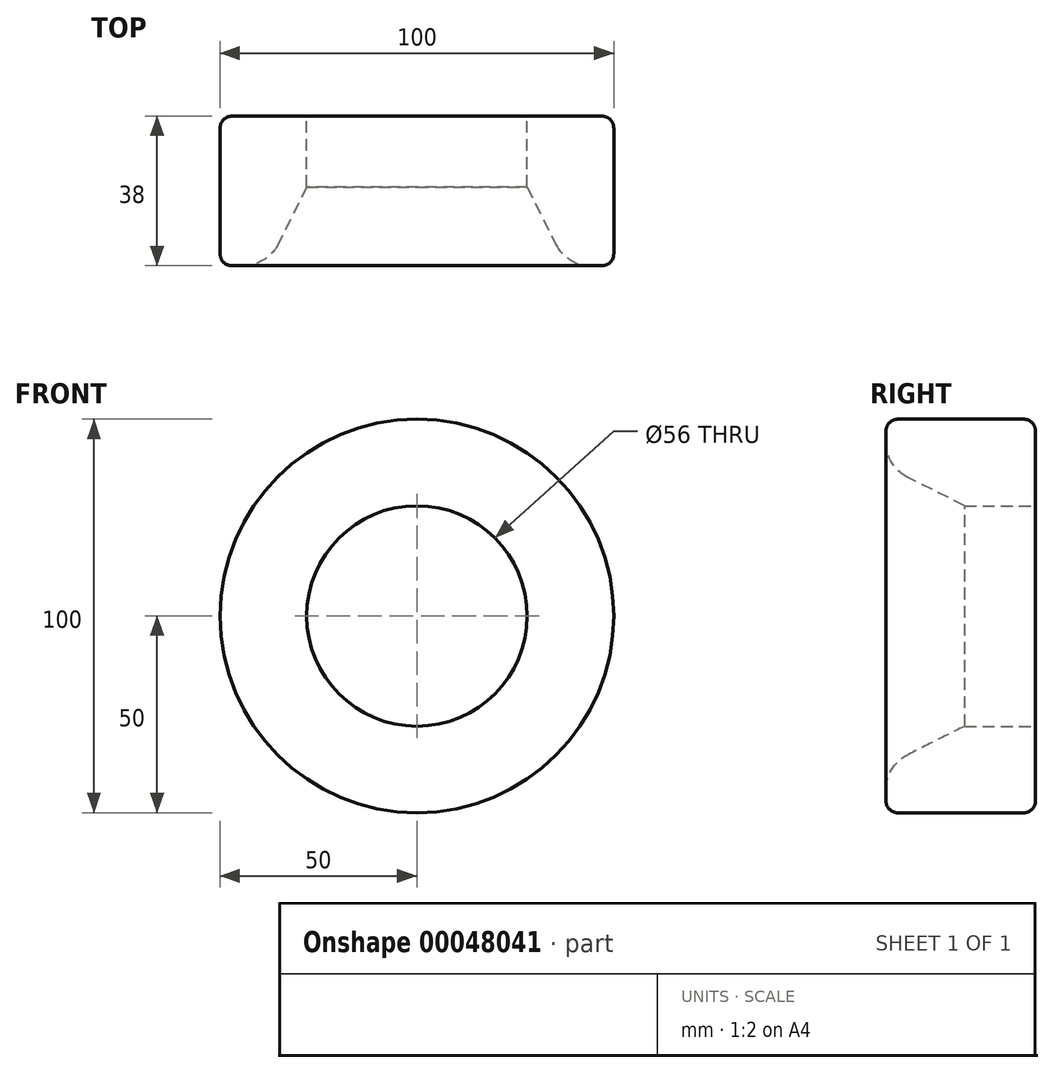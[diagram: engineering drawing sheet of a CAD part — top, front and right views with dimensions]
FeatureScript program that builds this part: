
annotation { "Feature Type Name" : "Feature", "Feature Type Description" : "" }
export const myFeature = defineFeature(function(context is Context, id is Id, definition is map)
    precondition{}
    {
        {
            var Q0;
            Q0=qCreatedBy(makeId("Front.planeOp"),FACE);
            var sketch = newSketch(context, id + "F0", { "sketchPlane" : qUnion([Q0])});
            skCircle(sketch, "E0", {"center": v(0, 0) * mm, "radius": 28 * mm});
            skCircle(sketch, "E1", {"center": v(0, 0) * mm, "radius": 50 * mm});
            skSolve(sketch);
        }
        {
            var Q0;
            Q0 = qSketchRegion(id + "F0", true);
            extrude(context, id + "F1", {"entities" : qUnion([Q0]), "depth" : 38 * mm});
        }
        {
            var Q0;
            Q0=makeQuery(id+"F1.opExtrude","CAP_EDGE",EDGE,{"disambiguationData":[OSD([sQuery(id+"F0.wireOp",EDGE,"E0")])],"isStart":false});
            chamfer(context, id + "F2", {"entities" : qUnion([Q0]), "chamferType" : ChamferType.TWO_OFFSETS, "width1" : 20 * mm, "oppositeDirection" : false, "width2" : 10 * mm, "tangentPropagation" : true});
        }
        {
            var Q0;
            {var subQ0=sQuery(id+"F0.wireOp",EDGE,"E0");Q0=makeQuery(id+"F2.opChamfer","BLEND_EDGE",EDGE,{"blendedFrom":[makeQuery(id+"F1.opExtrude","CAP_EDGE",EDGE,{"disambiguationData":[OSD([subQ0])],"isStart":false}),makeQuery(id+"F1.opExtrude","CAP_FACE",FACE,{"disambiguationData":[OSD([subQ0,sQuery(id+"F0.wireOp",EDGE,"E1")])],"isStart":false})],"blendedInto":[makeQuery(id+"F1.opExtrude","CAP_FACE",FACE,{"disambiguationData":[OSD([subQ0,sQuery(id+"F0.wireOp",EDGE,"E1")])],"isStart":false})]});}
            fillet(context, id + "F3", {"entities" : qUnion([Q0]), "radius" : 10 * mm, "tangentPropagation" : true, "allowEdgeOverflow" : false});
        }
        {
            var Q0;
            Q0=makeQuery(id+"F1.opExtrude","CAP_EDGE",EDGE,{"disambiguationData":[OSD([sQuery(id+"F0.wireOp",EDGE,"E1")])],"isStart":true});
            var Q1;
            Q1=makeQuery(id+"F1.opExtrude","CAP_EDGE",EDGE,{"disambiguationData":[OSD([sQuery(id+"F0.wireOp",EDGE,"E1")])],"isStart":false});
            fillet(context, id + "F4", {"entities" : qUnion([Q0, Q1]), "radius" : 3 * mm, "tangentPropagation" : true, "allowEdgeOverflow" : false});
        }
    });
